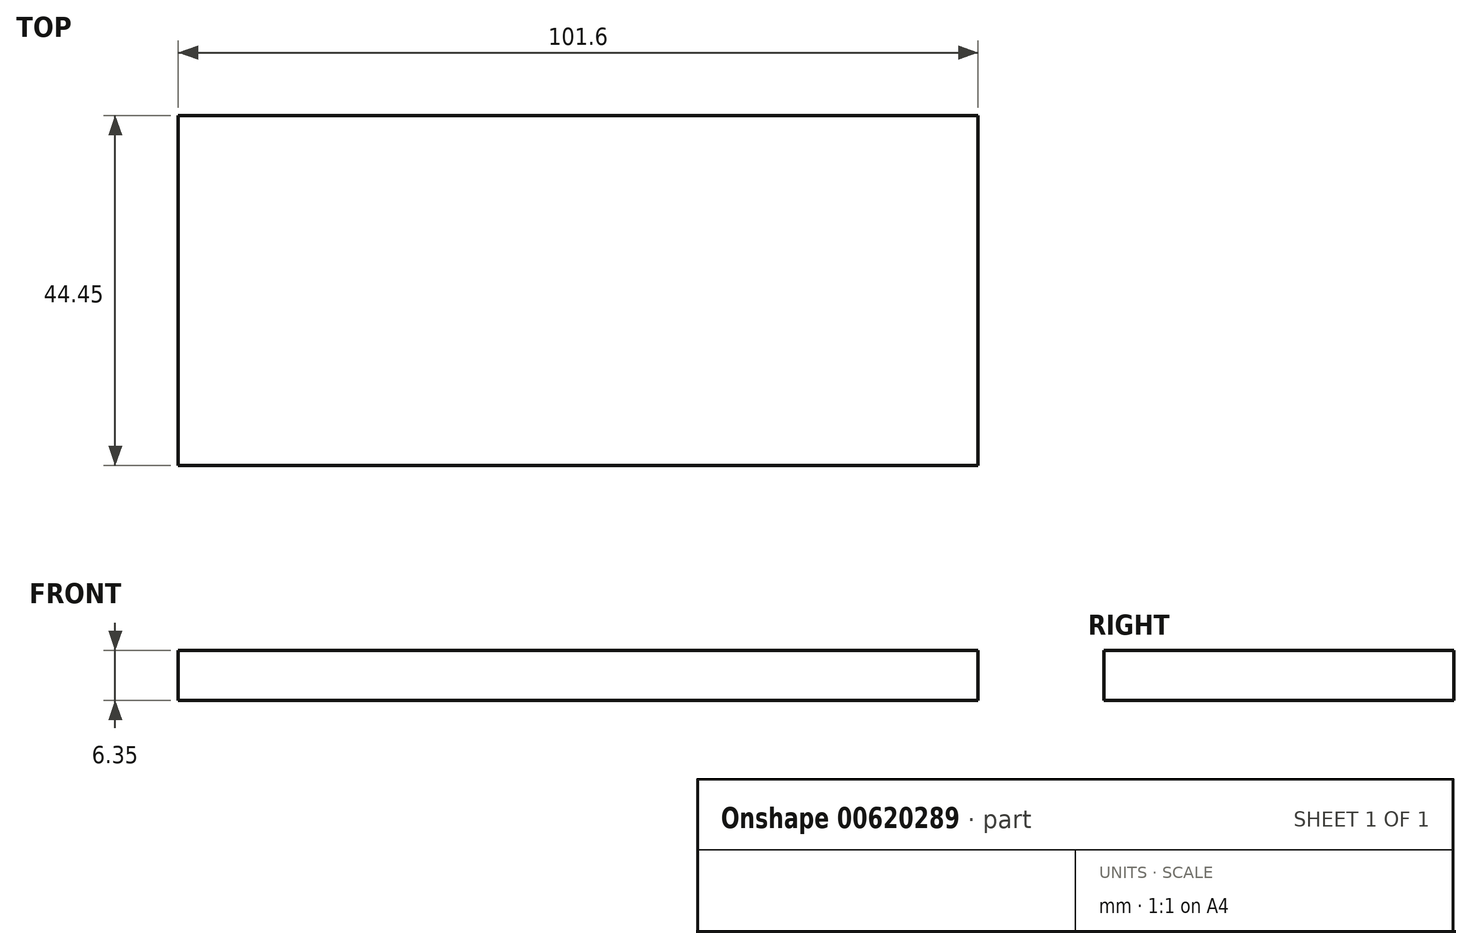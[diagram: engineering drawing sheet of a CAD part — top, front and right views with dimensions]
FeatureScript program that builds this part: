
annotation { "Feature Type Name" : "Feature", "Feature Type Description" : "" }
export const myFeature = defineFeature(function(context is Context, id is Id, definition is map)
    precondition{}
    {
        {
            var Q0;
            Q0=qCreatedBy(makeId("Top.planeOp"),FACE);
            var sketch = newSketch(context, id + "F0", { "sketchPlane" : qUnion([Q0])});
            skLineSegment(sketch, "E0.bottom", {"start": v(47.68, 8.74) * mm, "end": v(-53.92, 8.74) * mm});
            skLineSegment(sketch, "E0.top", {"start": v(47.68, -35.71) * mm, "end": v(-53.92, -35.71) * mm});
            skLineSegment(sketch, "E0.left", {"start": v(47.68, 8.74) * mm, "end": v(47.68, -35.71) * mm});
            skLineSegment(sketch, "E0.right", {"start": v(-53.92, 8.74) * mm, "end": v(-53.92, -35.71) * mm});
            skSolve(sketch);
        }
        {
            var Q0;
            Q0 = qSketchRegion(id + "F0", true);
            extrude(context, id + "F1", {"entities" : qUnion([Q0]), "depth" : 6.35 * mm, "offsetDistance" : 25.4 * mm});
        }
    });
